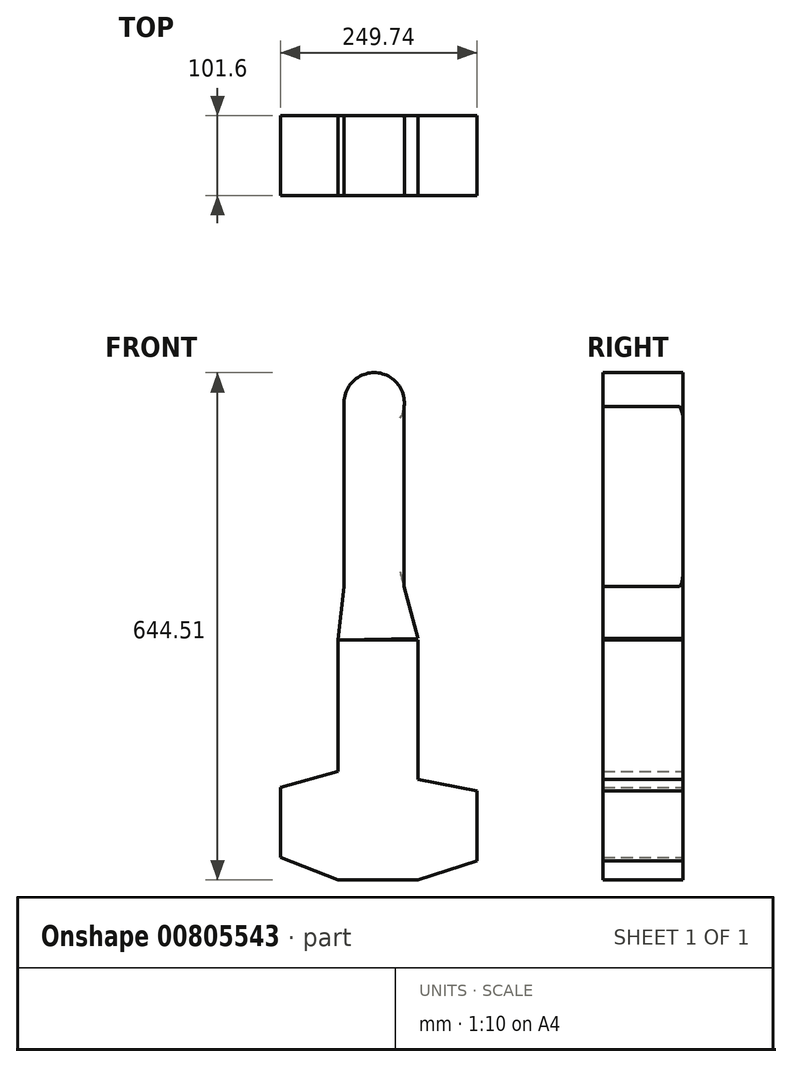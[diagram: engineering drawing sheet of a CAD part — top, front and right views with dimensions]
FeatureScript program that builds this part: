
annotation { "Feature Type Name" : "Feature", "Feature Type Description" : "" }
export const myFeature = defineFeature(function(context is Context, id is Id, definition is map)
    precondition{}
    {
        {
            var Q0;
            Q0=qCreatedBy(makeId("Front.planeOp"),FACE);
            var sketch = newSketch(context, id + "F0", { "sketchPlane" : qUnion([Q0])});
            skLineSegment(sketch, "E0.bottom", {"start": v(-36.77, 109.62) * mm, "end": v(39.43, 109.62) * mm});
            skLineSegment(sketch, "E0.top", {"start": v(-36.77, -118.98) * mm, "end": v(39.43, -118.98) * mm});
            skLineSegment(sketch, "E0.left", {"start": v(-36.77, 109.62) * mm, "end": v(-36.77, -118.98) * mm});
            skLineSegment(sketch, "E0.right", {"start": v(39.43, 109.62) * mm, "end": v(39.43, -118.98) * mm});
            skArc(sketch, "E1", {"start": v(39.43, 109.62) * mm, "mid": v(1.33, 152.57) * mm, "end": v(-36.77, 109.62) * mm});
            skLineSegment(sketch, "E2", {"start": v(-36.77, -118.98) * mm, "end": v(-44.4, -187.14) * mm});
            skLineSegment(sketch, "E3", {"start": v(39.43, -118.98) * mm, "end": v(57.19, -185.22) * mm});
            skLineSegment(sketch, "E4.bottom", {"start": v(-44.4, -187.14) * mm, "end": v(57.2, -187.14) * mm});
            skLineSegment(sketch, "E4.top", {"start": v(-44.4, -491.94) * mm, "end": v(57.2, -491.94) * mm});
            skLineSegment(sketch, "E4.left", {"start": v(-44.4, -187.14) * mm, "end": v(-44.4, -491.94) * mm});
            skLineSegment(sketch, "E4.right", {"start": v(57.2, -187.14) * mm, "end": v(57.2, -491.94) * mm});
            skLineSegment(sketch, "E5", {"start": v(-44.4, -187.14) * mm, "end": v(57.19, -185.22) * mm});
            skLineSegment(sketch, "E6", {"start": v(-44.4, -353.78) * mm, "end": v(-117.72, -374.52) * mm});
            skLineSegment(sketch, "E7", {"start": v(-117.72, -374.52) * mm, "end": v(-117.72, -463.42) * mm});
            skLineSegment(sketch, "E8", {"start": v(-117.72, -463.42) * mm, "end": v(-44.4, -491.94) * mm});
            skLineSegment(sketch, "E9", {"start": v(57.2, -364.25) * mm, "end": v(132.02, -378.73) * mm});
            skLineSegment(sketch, "E10", {"start": v(132.02, -378.73) * mm, "end": v(132.02, -467.63) * mm});
            skLineSegment(sketch, "E11", {"start": v(132.02, -467.63) * mm, "end": v(57.2, -491.94) * mm});
            skSolve(sketch);
        }
        {
            var Q0;
            Q0 = qSketchRegion(id + "F0", true);
            extrude(context, id + "F1", {"entities" : qUnion([Q0]), "depth" : 101.6 * mm, "offsetDistance" : 25.4 * mm});
        }
        {
            var Q0;
            Q0=makeQuery(id+"F1.opExtrude","CAP_EDGE",EDGE,{"disambiguationData":[OSD([sQuery(id+"F0.wireOp",EDGE,"E0.right")])],"isStart":true});
            fillet(context, id + "F2", {"entities" : qUnion([Q0]), "radius" : 5.08 * mm, "tangentPropagation" : true, "allowEdgeOverflow" : false});
        }
    });
